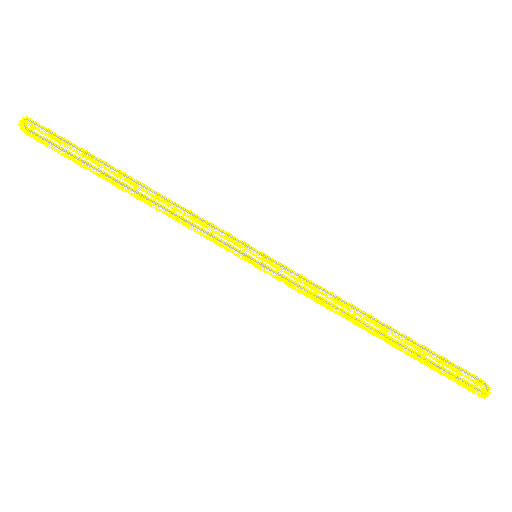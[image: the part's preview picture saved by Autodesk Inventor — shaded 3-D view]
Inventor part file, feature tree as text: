
AUTODESK INVENTOR PART (.ipt)
format: ipt  version: 2025.1 (Build 291241000, 241)  size: 7,385,600 bytes
history: native  units: mm
features: other x361, sketch x3, pattern_linear x2, extrude x2
ambient origin geometry x8: Origin, YZ Plane, XZ Plane, XY Plane, X Axis, Y Axis, Z Axis, Center Point
bodies: Body1 (feature_tree)
feature tree (368):
  other  "Bryła1"
  sketch  "Szkic1"
  other  "Punkt konstrukcyjny1"
  pattern_linear  "Szyk prostokątny1"  Spacing1=27.95mm  [1 undecoded]
  extrude  "Wyciągnięcie proste1"  Depth=1439.872mm
  pattern_linear  "Szyk prostokątny2"  Count1=360 Spacing1=10.0mm
  extrude  "Wyciągnięcie proste2"  Depth=1.0mm
  other  "Punkt konstrukcyjny2"
  other  "Punkt konstrukcyjny3"
  other  "Punkt konstrukcyjny4"
  other  "Punkt konstrukcyjny5"
  other  "Punkt konstrukcyjny6"
  other  "Punkt konstrukcyjny7"
  other  "Punkt konstrukcyjny8"
  other  "Punkt konstrukcyjny9"
  other  "Punkt konstrukcyjny10"
  other  "Punkt konstrukcyjny11"
  other  "Punkt konstrukcyjny12"
  other  "Punkt konstrukcyjny13"
  other  "Punkt konstrukcyjny14"
  other  "Punkt konstrukcyjny15"
  other  "Punkt konstrukcyjny16"
  other  "Punkt konstrukcyjny17"
  other  "Punkt konstrukcyjny18"
  other  "Punkt konstrukcyjny19"
  other  "Punkt konstrukcyjny20"
  other  "Punkt konstrukcyjny21"
  other  "Punkt konstrukcyjny22"
  other  "Punkt konstrukcyjny23"
  other  "Punkt konstrukcyjny24"
  other  "Punkt konstrukcyjny25"
  other  "Punkt konstrukcyjny26"
  other  "Punkt konstrukcyjny27"
  other  "Punkt konstrukcyjny28"
  other  "Punkt konstrukcyjny29"
  other  "Punkt konstrukcyjny30"
  other  "Punkt konstrukcyjny31"
  other  "Punkt konstrukcyjny32"
  other  "Punkt konstrukcyjny33"
  other  "Punkt konstrukcyjny34"
  other  "Punkt konstrukcyjny35"
  other  "Punkt konstrukcyjny36"
  other  "Punkt konstrukcyjny37"
  other  "Punkt konstrukcyjny38"
  other  "Punkt konstrukcyjny39"
  other  "Punkt konstrukcyjny40"
  other  "Punkt konstrukcyjny41"
  other  "Punkt konstrukcyjny42"
  other  "Punkt konstrukcyjny43"
  other  "Punkt konstrukcyjny44"
  other  "Punkt konstrukcyjny45"
  other  "Punkt konstrukcyjny46"
  other  "Punkt konstrukcyjny47"
  other  "Punkt konstrukcyjny48"
  other  "Punkt konstrukcyjny49"
  other  "Punkt konstrukcyjny50"
  other  "Punkt konstrukcyjny51"
  other  "Punkt konstrukcyjny52"
  other  "Punkt konstrukcyjny53"
  other  "Punkt konstrukcyjny54"
  other  "Punkt konstrukcyjny55"
  other  "Punkt konstrukcyjny56"
  other  "Punkt konstrukcyjny57"
  other  "Punkt konstrukcyjny58"
  other  "Punkt konstrukcyjny59"
  other  "Punkt konstrukcyjny60"
  other  "Punkt konstrukcyjny61"
  other  "Punkt konstrukcyjny62"
  other  "Punkt konstrukcyjny63"
  other  "Punkt konstrukcyjny64"
  other  "Punkt konstrukcyjny65"
  other  "Punkt konstrukcyjny66"
  other  "Punkt konstrukcyjny67"
  other  "Punkt konstrukcyjny68"
  other  "Punkt konstrukcyjny69"
  other  "Punkt konstrukcyjny70"
  other  "Punkt konstrukcyjny71"
  other  "Punkt konstrukcyjny72"
  other  "Punkt konstrukcyjny73"
  other  "Punkt konstrukcyjny74"
  other  "Punkt konstrukcyjny75"
  other  "Punkt konstrukcyjny76"
  other  "Punkt konstrukcyjny77"
  other  "Punkt konstrukcyjny78"
  other  "Punkt konstrukcyjny79"
  other  "Punkt konstrukcyjny80"
  other  "Punkt konstrukcyjny81"
  other  "Punkt konstrukcyjny82"
  other  "Punkt konstrukcyjny83"
  other  "Punkt konstrukcyjny84"
  other  "Punkt konstrukcyjny85"
  other  "Punkt konstrukcyjny86"
  other  "Punkt konstrukcyjny87"
  other  "Punkt konstrukcyjny88"
  other  "Punkt konstrukcyjny89"
  other  "Punkt konstrukcyjny90"
  other  "Punkt konstrukcyjny91"
  other  "Punkt konstrukcyjny92"
  other  "Punkt konstrukcyjny93"
  other  "Punkt konstrukcyjny94"
  other  "Punkt konstrukcyjny95"
  other  "Punkt konstrukcyjny96"
  other  "Punkt konstrukcyjny97"
  other  "Punkt konstrukcyjny98"
  other  "Punkt konstrukcyjny99"
  other  "Punkt konstrukcyjny100"
  other  "Punkt konstrukcyjny101"
  other  "Punkt konstrukcyjny102"
  other  "Punkt konstrukcyjny103"
  other  "Punkt konstrukcyjny104"
  other  "Punkt konstrukcyjny105"
  other  "Punkt konstrukcyjny106"
  other  "Punkt konstrukcyjny107"
  other  "Punkt konstrukcyjny108"
  other  "Punkt konstrukcyjny109"
  other  "Punkt konstrukcyjny110"
  other  "Punkt konstrukcyjny111"
  other  "Punkt konstrukcyjny112"
  other  "Punkt konstrukcyjny113"
  other  "Punkt konstrukcyjny114"
  other  "Punkt konstrukcyjny115"
  other  "Punkt konstrukcyjny116"
  other  "Punkt konstrukcyjny117"
  other  "Punkt konstrukcyjny118"
  other  "Punkt konstrukcyjny119"
  other  "Punkt konstrukcyjny120"
  other  "Punkt konstrukcyjny121"
  other  "Punkt konstrukcyjny122"
  other  "Punkt konstrukcyjny123"
  other  "Punkt konstrukcyjny124"
  other  "Punkt konstrukcyjny125"
  other  "Punkt konstrukcyjny126"
  other  "Punkt konstrukcyjny127"
  other  "Punkt konstrukcyjny128"
  other  "Punkt konstrukcyjny129"
  other  "Punkt konstrukcyjny130"
  other  "Punkt konstrukcyjny131"
  other  "Punkt konstrukcyjny132"
  other  "Punkt konstrukcyjny133"
  other  "Punkt konstrukcyjny134"
  other  "Punkt konstrukcyjny135"
  other  "Punkt konstrukcyjny136"
  other  "Punkt konstrukcyjny137"
  other  "Punkt konstrukcyjny138"
  other  "Punkt konstrukcyjny139"
  other  "Punkt konstrukcyjny140"
  other  "Punkt konstrukcyjny141"
  other  "Punkt konstrukcyjny142"
  other  "Punkt konstrukcyjny143"
  other  "Punkt konstrukcyjny144"
  other  "Punkt konstrukcyjny145"
  other  "Punkt konstrukcyjny146"
  other  "Punkt konstrukcyjny147"
  other  "Punkt konstrukcyjny148"
  other  "Punkt konstrukcyjny149"
  other  "Punkt konstrukcyjny150"
  other  "Punkt konstrukcyjny151"
  other  "Punkt konstrukcyjny152"
  other  "Punkt konstrukcyjny153"
  other  "Punkt konstrukcyjny154"
  other  "Punkt konstrukcyjny155"
  other  "Punkt konstrukcyjny156"
  other  "Punkt konstrukcyjny157"
  other  "Punkt konstrukcyjny158"
  other  "Punkt konstrukcyjny159"
  other  "Punkt konstrukcyjny160"
  other  "Punkt konstrukcyjny161"
  other  "Punkt konstrukcyjny162"
  other  "Punkt konstrukcyjny163"
  other  "Punkt konstrukcyjny164"
  other  "Punkt konstrukcyjny165"
  other  "Punkt konstrukcyjny166"
  other  "Punkt konstrukcyjny167"
  other  "Punkt konstrukcyjny168"
  other  "Punkt konstrukcyjny169"
  other  "Punkt konstrukcyjny170"
  other  "Punkt konstrukcyjny171"
  other  "Punkt konstrukcyjny172"
  other  "Punkt konstrukcyjny173"
  other  "Punkt konstrukcyjny174"
  other  "Punkt konstrukcyjny175"
  other  "Punkt konstrukcyjny176"
  other  "Punkt konstrukcyjny177"
  other  "Punkt konstrukcyjny178"
  other  "Punkt konstrukcyjny179"
  other  "Punkt konstrukcyjny180"
  other  "Punkt konstrukcyjny181"
  other  "Punkt konstrukcyjny182"
  other  "Punkt konstrukcyjny183"
  other  "Punkt konstrukcyjny184"
  other  "Punkt konstrukcyjny185"
  other  "Punkt konstrukcyjny186"
  other  "Punkt konstrukcyjny187"
  other  "Punkt konstrukcyjny188"
  other  "Punkt konstrukcyjny189"
  other  "Punkt konstrukcyjny190"
  other  "Punkt konstrukcyjny191"
  other  "Punkt konstrukcyjny192"
  other  "Punkt konstrukcyjny193"
  other  "Punkt konstrukcyjny194"
  other  "Punkt konstrukcyjny195"
  other  "Punkt konstrukcyjny196"
  other  "Punkt konstrukcyjny197"
  other  "Punkt konstrukcyjny198"
  other  "Punkt konstrukcyjny199"
  other  "Punkt konstrukcyjny200"
  other  "Punkt konstrukcyjny201"
  other  "Punkt konstrukcyjny202"
  other  "Punkt konstrukcyjny203"
  other  "Punkt konstrukcyjny204"
  other  "Punkt konstrukcyjny205"
  other  "Punkt konstrukcyjny206"
  other  "Punkt konstrukcyjny207"
  other  "Punkt konstrukcyjny208"
  other  "Punkt konstrukcyjny209"
  other  "Punkt konstrukcyjny210"
  other  "Punkt konstrukcyjny211"
  other  "Punkt konstrukcyjny212"
  other  "Punkt konstrukcyjny213"
  other  "Punkt konstrukcyjny214"
  other  "Punkt konstrukcyjny215"
  other  "Punkt konstrukcyjny216"
  other  "Punkt konstrukcyjny217"
  other  "Punkt konstrukcyjny218"
  other  "Punkt konstrukcyjny219"
  other  "Punkt konstrukcyjny220"
  other  "Punkt konstrukcyjny221"
  other  "Punkt konstrukcyjny222"
  other  "Punkt konstrukcyjny223"
  other  "Punkt konstrukcyjny224"
  other  "Punkt konstrukcyjny225"
  other  "Punkt konstrukcyjny226"
  other  "Punkt konstrukcyjny227"
  other  "Punkt konstrukcyjny228"
  other  "Punkt konstrukcyjny229"
  other  "Punkt konstrukcyjny230"
  other  "Punkt konstrukcyjny231"
  other  "Punkt konstrukcyjny232"
  other  "Punkt konstrukcyjny233"
  other  "Punkt konstrukcyjny234"
  other  "Punkt konstrukcyjny235"
  other  "Punkt konstrukcyjny236"
  other  "Punkt konstrukcyjny237"
  other  "Punkt konstrukcyjny238"
  other  "Punkt konstrukcyjny239"
  other  "Punkt konstrukcyjny240"
  other  "Punkt konstrukcyjny241"
  other  "Punkt konstrukcyjny242"
  other  "Punkt konstrukcyjny243"
  other  "Punkt konstrukcyjny244"
  other  "Punkt konstrukcyjny245"
  other  "Punkt konstrukcyjny246"
  other  "Punkt konstrukcyjny247"
  other  "Punkt konstrukcyjny248"
  other  "Punkt konstrukcyjny249"
  other  "Punkt konstrukcyjny250"
  other  "Punkt konstrukcyjny251"
  other  "Punkt konstrukcyjny252"
  other  "Punkt konstrukcyjny253"
  other  "Punkt konstrukcyjny254"
  other  "Punkt konstrukcyjny255"
  other  "Punkt konstrukcyjny256"
  other  "Punkt konstrukcyjny257"
  other  "Punkt konstrukcyjny258"
  other  "Punkt konstrukcyjny259"
  other  "Punkt konstrukcyjny260"
  other  "Punkt konstrukcyjny261"
  other  "Punkt konstrukcyjny262"
  other  "Punkt konstrukcyjny263"
  other  "Punkt konstrukcyjny264"
  other  "Punkt konstrukcyjny265"
  other  "Punkt konstrukcyjny266"
  other  "Punkt konstrukcyjny267"
  other  "Punkt konstrukcyjny268"
  other  "Punkt konstrukcyjny269"
  other  "Punkt konstrukcyjny270"
  other  "Punkt konstrukcyjny271"
  other  "Punkt konstrukcyjny272"
  other  "Punkt konstrukcyjny273"
  other  "Punkt konstrukcyjny274"
  other  "Punkt konstrukcyjny275"
  other  "Punkt konstrukcyjny276"
  other  "Punkt konstrukcyjny277"
  other  "Punkt konstrukcyjny278"
  other  "Punkt konstrukcyjny279"
  other  "Punkt konstrukcyjny280"
  other  "Punkt konstrukcyjny281"
  other  "Punkt konstrukcyjny282"
  other  "Punkt konstrukcyjny283"
  other  "Punkt konstrukcyjny284"
  other  "Punkt konstrukcyjny285"
  other  "Punkt konstrukcyjny286"
  other  "Punkt konstrukcyjny287"
  other  "Punkt konstrukcyjny288"
  other  "Punkt konstrukcyjny289"
  other  "Punkt konstrukcyjny290"
  other  "Punkt konstrukcyjny291"
  other  "Punkt konstrukcyjny292"
  other  "Punkt konstrukcyjny293"
  other  "Punkt konstrukcyjny294"
  other  "Punkt konstrukcyjny295"
  other  "Punkt konstrukcyjny296"
  other  "Punkt konstrukcyjny297"
  other  "Punkt konstrukcyjny298"
  other  "Punkt konstrukcyjny299"
  other  "Punkt konstrukcyjny300"
  other  "Punkt konstrukcyjny301"
  other  "Punkt konstrukcyjny302"
  other  "Punkt konstrukcyjny303"
  other  "Punkt konstrukcyjny304"
  other  "Punkt konstrukcyjny305"
  other  "Punkt konstrukcyjny306"
  other  "Punkt konstrukcyjny307"
  other  "Punkt konstrukcyjny308"
  other  "Punkt konstrukcyjny309"
  other  "Punkt konstrukcyjny310"
  other  "Punkt konstrukcyjny311"
  other  "Punkt konstrukcyjny312"
  other  "Punkt konstrukcyjny313"
  other  "Punkt konstrukcyjny314"
  other  "Punkt konstrukcyjny315"
  other  "Punkt konstrukcyjny316"
  other  "Punkt konstrukcyjny317"
  other  "Punkt konstrukcyjny318"
  other  "Punkt konstrukcyjny319"
  other  "Punkt konstrukcyjny320"
  other  "Punkt konstrukcyjny321"
  other  "Punkt konstrukcyjny322"
  other  "Punkt konstrukcyjny323"
  other  "Punkt konstrukcyjny324"
  other  "Punkt konstrukcyjny325"
  other  "Punkt konstrukcyjny326"
  other  "Punkt konstrukcyjny327"
  other  "Punkt konstrukcyjny328"
  other  "Punkt konstrukcyjny329"
  other  "Punkt konstrukcyjny330"
  other  "Punkt konstrukcyjny331"
  other  "Punkt konstrukcyjny332"
  other  "Punkt konstrukcyjny333"
  other  "Punkt konstrukcyjny334"
  other  "Punkt konstrukcyjny335"
  other  "Punkt konstrukcyjny336"
  other  "Punkt konstrukcyjny337"
  other  "Punkt konstrukcyjny338"
  other  "Punkt konstrukcyjny339"
  other  "Punkt konstrukcyjny340"
  other  "Punkt konstrukcyjny341"
  other  "Punkt konstrukcyjny342"
  other  "Punkt konstrukcyjny343"
  other  "Punkt konstrukcyjny344"
  other  "Punkt konstrukcyjny345"
  other  "Punkt konstrukcyjny346"
  other  "Punkt konstrukcyjny347"
  other  "Punkt konstrukcyjny348"
  other  "Punkt konstrukcyjny349"
  other  "Punkt konstrukcyjny350"
  other  "Punkt konstrukcyjny351"
  other  "Punkt konstrukcyjny352"
  other  "Punkt konstrukcyjny353"
  other  "Punkt konstrukcyjny354"
  other  "Punkt konstrukcyjny355"
  other  "Punkt konstrukcyjny356"
  other  "Punkt konstrukcyjny357"
  other  "Punkt konstrukcyjny358"
  other  "Punkt konstrukcyjny359"
  other  "Punkt konstrukcyjny360"
  sketch  "Szkic6"
  sketch  "Szkic7"
note: 1 required parameter value undecoded (feature->parameter linkage not recoverable at this tier; creation-order binding heuristic only, values carry confidence <= 0.55)
